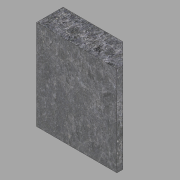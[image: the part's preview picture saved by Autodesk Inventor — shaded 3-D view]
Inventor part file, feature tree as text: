
AUTODESK INVENTOR PART (.ipt)
format: ipt  version: 2022.2 (Build 262287000, 287)  size: 128,000 bytes
history: native  units: in
note: dims shown in document units (in); Inventor stores cm internally (conversion verified against a paired STEP export)
features: extrude x2, sketch x2
ambient origin geometry x8: Origin, YZ Plane, XZ Plane, XY Plane, X Axis, Y Axis, Z Axis, Center Point
bodies: Solid1 (feature_tree)
feature tree (4):
  extrude  "Extrusion1"  Depth=7.625in
  extrude  "Extrusion3"  TaperAngle=45.0deg  [1 undecoded]
  sketch  "Sketch1"  dims[d0=2.25in d1=7.625in]
  sketch  "Sketch3"  dims[d2=6.8125in d3=0.0in d9=45.0deg d10=0.5in d11=1.75in d12=1.0in d13=0.0in]
note: 1 required parameter value undecoded (feature->parameter linkage not recoverable at this tier; creation-order binding heuristic only, values carry confidence <= 0.55)
